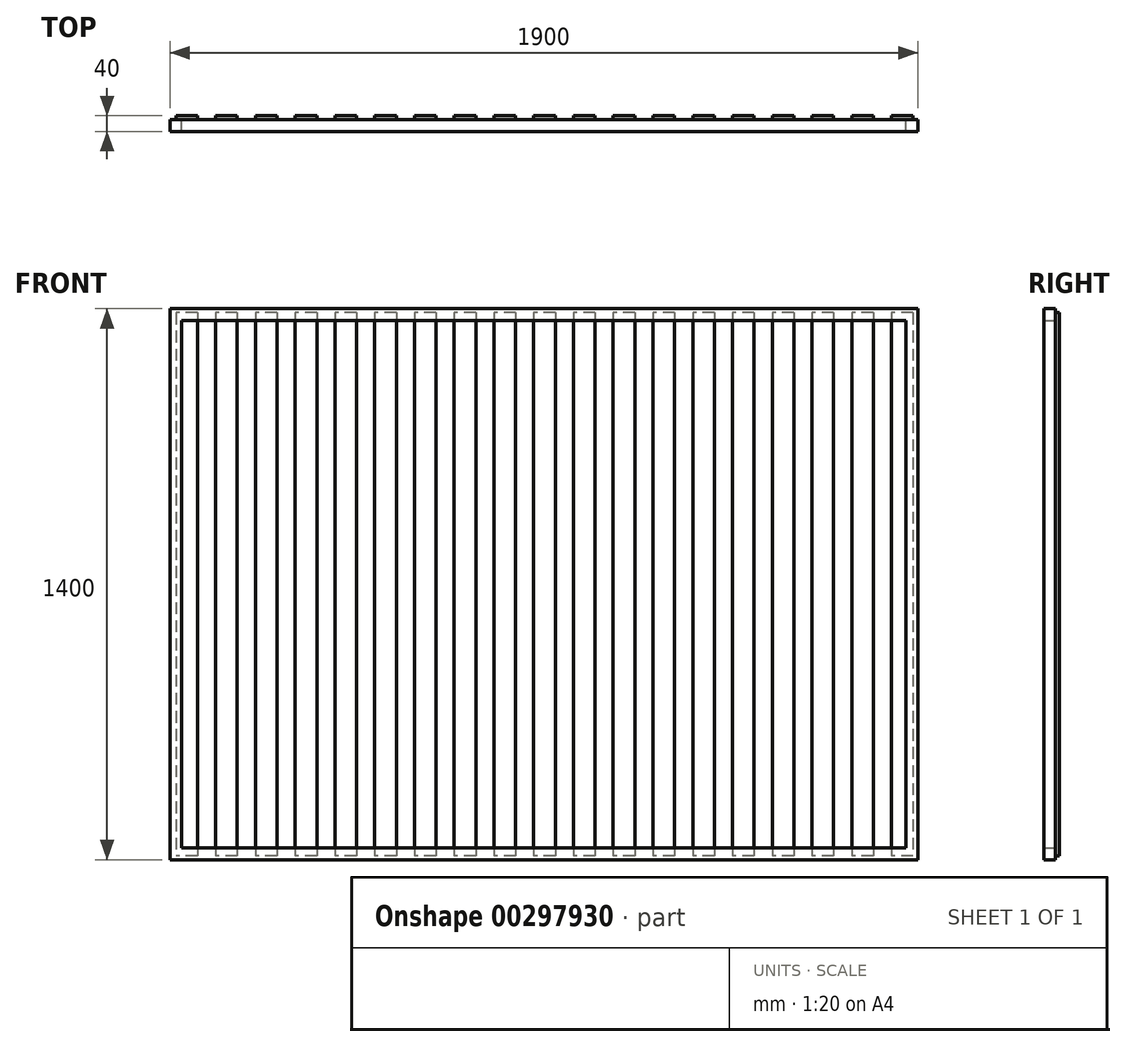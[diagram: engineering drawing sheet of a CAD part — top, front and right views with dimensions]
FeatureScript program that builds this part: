
annotation { "Feature Type Name" : "Feature", "Feature Type Description" : "" }
export const myFeature = defineFeature(function(context is Context, id is Id, definition is map)
    precondition{}
    {
        {
            var Q0;
            Q0=qCreatedBy(makeId("Front.planeOp"),FACE);
            var sketch = newSketch(context, id + "F0", { "sketchPlane" : qUnion([Q0])});
            skLineSegment(sketch, "E0.bottom", {"start": v(950, 700) * mm, "end": v(-950, 700) * mm});
            skLineSegment(sketch, "E0.top", {"start": v(950, -700) * mm, "end": v(-950, -700) * mm});
            skLineSegment(sketch, "E0.left", {"start": v(950, 700) * mm, "end": v(950, -700) * mm});
            skLineSegment(sketch, "E0.right", {"start": v(-950, 700) * mm, "end": v(-950, -700) * mm});
            skPoint(sketch, "E0.middle", {"position": v(0, 0) * mm});
            skLineSegment(sketch, "E1.bottom", {"start": v(-920, 670) * mm, "end": v(920, 670) * mm});
            skLineSegment(sketch, "E1.top", {"start": v(-920, -670) * mm, "end": v(920, -670) * mm});
            skLineSegment(sketch, "E1.left", {"start": v(-920, 670) * mm, "end": v(-920, -670) * mm});
            skLineSegment(sketch, "E1.right", {"start": v(920, 670) * mm, "end": v(920, -670) * mm});
            skSolve(sketch);
        }
        {
            var Q0;
            Q0=makeQuery(id+"F0.imprint","IMPRINT",FACE,{"disambiguationData":[TD([[makeQuery(id+"F0.imprint","IMPRINT",EDGE,{"derivedFrom":sQuery(id+"F0.wireOp",EDGE,"E0.bottom")}),1.0]])]});
            extrude(context, id + "F1", {"entities" : qUnion([Q0]), "endBound" : BoundingType.SYMMETRIC, "depth" : 30 * mm});
        }
        {
            var Q0;
            Q0=qCreatedBy(makeId("Top.planeOp"),FACE);
            var sketch = newSketch(context, id + "F2", { "sketchPlane" : qUnion([Q0])});
            skLineSegment(sketch, "E2.bottom", {"start": v(-880, 25) * mm, "end": v(-935, 25) * mm});
            skLineSegment(sketch, "E2.top", {"start": v(-880, 15) * mm, "end": v(-935, 15) * mm});
            skLineSegment(sketch, "E2.left", {"start": v(-880, 25) * mm, "end": v(-880, 15) * mm});
            skLineSegment(sketch, "E2.right", {"start": v(-935, 25) * mm, "end": v(-935, 15) * mm});
            skPoint(sketch, "E2.middle", {"position": v(-907.5, 20) * mm});
            skLineSegment(sketch, "E3.1.0.0", {"start": v(-834, 25) * mm, "end": v(-834, 15) * mm});
            skLineSegment(sketch, "E3.1.0.1", {"start": v(-779, 25) * mm, "end": v(-779, 15) * mm});
            skLineSegment(sketch, "E3.1.0.2", {"start": v(-779, 15) * mm, "end": v(-834, 15) * mm});
            skLineSegment(sketch, "E3.1.0.3", {"start": v(-779, 25) * mm, "end": v(-834, 25) * mm});
            skPoint(sketch, "E3.1.0.4", {"position": v(-806.5, 20) * mm});
            skLineSegment(sketch, "E3.2.0.0", {"start": v(-733, 25) * mm, "end": v(-733, 15) * mm});
            skLineSegment(sketch, "E3.2.0.1", {"start": v(-678, 25) * mm, "end": v(-678, 15) * mm});
            skLineSegment(sketch, "E3.2.0.2", {"start": v(-678, 15) * mm, "end": v(-733, 15) * mm});
            skLineSegment(sketch, "E3.2.0.3", {"start": v(-678, 25) * mm, "end": v(-733, 25) * mm});
            skPoint(sketch, "E3.2.0.4", {"position": v(-705.5, 20) * mm});
            skLineSegment(sketch, "E3.3.0.0", {"start": v(-632, 25) * mm, "end": v(-632, 15) * mm});
            skLineSegment(sketch, "E3.3.0.1", {"start": v(-577, 25) * mm, "end": v(-577, 15) * mm});
            skLineSegment(sketch, "E3.3.0.2", {"start": v(-577, 15) * mm, "end": v(-632, 15) * mm});
            skLineSegment(sketch, "E3.3.0.3", {"start": v(-577, 25) * mm, "end": v(-632, 25) * mm});
            skPoint(sketch, "E3.3.0.4", {"position": v(-604.5, 20) * mm});
            skLineSegment(sketch, "E3.4.0.0", {"start": v(-531, 25) * mm, "end": v(-531, 15) * mm});
            skLineSegment(sketch, "E3.4.0.1", {"start": v(-476, 25) * mm, "end": v(-476, 15) * mm});
            skLineSegment(sketch, "E3.4.0.2", {"start": v(-476, 15) * mm, "end": v(-531, 15) * mm});
            skLineSegment(sketch, "E3.4.0.3", {"start": v(-476, 25) * mm, "end": v(-531, 25) * mm});
            skPoint(sketch, "E3.4.0.4", {"position": v(-503.5, 20) * mm});
            skLineSegment(sketch, "E3.5.0.0", {"start": v(-430, 25) * mm, "end": v(-430, 15) * mm});
            skLineSegment(sketch, "E3.5.0.1", {"start": v(-375, 25) * mm, "end": v(-375, 15) * mm});
            skLineSegment(sketch, "E3.5.0.2", {"start": v(-375, 15) * mm, "end": v(-430, 15) * mm});
            skLineSegment(sketch, "E3.5.0.3", {"start": v(-375, 25) * mm, "end": v(-430, 25) * mm});
            skPoint(sketch, "E3.5.0.4", {"position": v(-402.5, 20) * mm});
            skLineSegment(sketch, "E3.6.0.0", {"start": v(-329, 25) * mm, "end": v(-329, 15) * mm});
            skLineSegment(sketch, "E3.6.0.1", {"start": v(-274, 25) * mm, "end": v(-274, 15) * mm});
            skLineSegment(sketch, "E3.6.0.2", {"start": v(-274, 15) * mm, "end": v(-329, 15) * mm});
            skLineSegment(sketch, "E3.6.0.3", {"start": v(-274, 25) * mm, "end": v(-329, 25) * mm});
            skPoint(sketch, "E3.6.0.4", {"position": v(-301.5, 20) * mm});
            skLineSegment(sketch, "E3.7.0.0", {"start": v(-228, 25) * mm, "end": v(-228, 15) * mm});
            skLineSegment(sketch, "E3.7.0.1", {"start": v(-173, 25) * mm, "end": v(-173, 15) * mm});
            skLineSegment(sketch, "E3.7.0.2", {"start": v(-173, 15) * mm, "end": v(-228, 15) * mm});
            skLineSegment(sketch, "E3.7.0.3", {"start": v(-173, 25) * mm, "end": v(-228, 25) * mm});
            skPoint(sketch, "E3.7.0.4", {"position": v(-200.5, 20) * mm});
            skLineSegment(sketch, "E3.8.0.0", {"start": v(-127, 25) * mm, "end": v(-127, 15) * mm});
            skLineSegment(sketch, "E3.8.0.1", {"start": v(-72, 25) * mm, "end": v(-72, 15) * mm});
            skLineSegment(sketch, "E3.8.0.2", {"start": v(-72, 15) * mm, "end": v(-127, 15) * mm});
            skLineSegment(sketch, "E3.8.0.3", {"start": v(-72, 25) * mm, "end": v(-127, 25) * mm});
            skPoint(sketch, "E3.8.0.4", {"position": v(-99.5, 20) * mm});
            skLineSegment(sketch, "E3.9.0.0", {"start": v(-26, 25) * mm, "end": v(-26, 15) * mm});
            skLineSegment(sketch, "E3.9.0.1", {"start": v(29, 25) * mm, "end": v(29, 15) * mm});
            skLineSegment(sketch, "E3.9.0.2", {"start": v(29, 15) * mm, "end": v(-26, 15) * mm});
            skLineSegment(sketch, "E3.9.0.3", {"start": v(29, 25) * mm, "end": v(-26, 25) * mm});
            skPoint(sketch, "E3.9.0.4", {"position": v(1.5, 20) * mm});
            skLineSegment(sketch, "E3.10.0.0", {"start": v(75, 25) * mm, "end": v(75, 15) * mm});
            skLineSegment(sketch, "E3.10.0.1", {"start": v(130, 25) * mm, "end": v(130, 15) * mm});
            skLineSegment(sketch, "E3.10.0.2", {"start": v(130, 15) * mm, "end": v(75, 15) * mm});
            skLineSegment(sketch, "E3.10.0.3", {"start": v(130, 25) * mm, "end": v(75, 25) * mm});
            skPoint(sketch, "E3.10.0.4", {"position": v(102.5, 20) * mm});
            skLineSegment(sketch, "E3.11.0.0", {"start": v(176, 25) * mm, "end": v(176, 15) * mm});
            skLineSegment(sketch, "E3.11.0.1", {"start": v(231, 25) * mm, "end": v(231, 15) * mm});
            skLineSegment(sketch, "E3.11.0.2", {"start": v(231, 15) * mm, "end": v(176, 15) * mm});
            skLineSegment(sketch, "E3.11.0.3", {"start": v(231, 25) * mm, "end": v(176, 25) * mm});
            skPoint(sketch, "E3.11.0.4", {"position": v(203.5, 20) * mm});
            skLineSegment(sketch, "E3.12.0.0", {"start": v(277, 25) * mm, "end": v(277, 15) * mm});
            skLineSegment(sketch, "E3.12.0.1", {"start": v(332, 25) * mm, "end": v(332, 15) * mm});
            skLineSegment(sketch, "E3.12.0.2", {"start": v(332, 15) * mm, "end": v(277, 15) * mm});
            skLineSegment(sketch, "E3.12.0.3", {"start": v(332, 25) * mm, "end": v(277, 25) * mm});
            skPoint(sketch, "E3.12.0.4", {"position": v(304.5, 20) * mm});
            skLineSegment(sketch, "E3.13.0.0", {"start": v(378, 25) * mm, "end": v(378, 15) * mm});
            skLineSegment(sketch, "E3.13.0.1", {"start": v(433, 25) * mm, "end": v(433, 15) * mm});
            skLineSegment(sketch, "E3.13.0.2", {"start": v(433, 15) * mm, "end": v(378, 15) * mm});
            skLineSegment(sketch, "E3.13.0.3", {"start": v(433, 25) * mm, "end": v(378, 25) * mm});
            skPoint(sketch, "E3.13.0.4", {"position": v(405.5, 20) * mm});
            skLineSegment(sketch, "E3.14.0.0", {"start": v(479, 25) * mm, "end": v(479, 15) * mm});
            skLineSegment(sketch, "E3.14.0.1", {"start": v(534, 25) * mm, "end": v(534, 15) * mm});
            skLineSegment(sketch, "E3.14.0.2", {"start": v(534, 15) * mm, "end": v(479, 15) * mm});
            skLineSegment(sketch, "E3.14.0.3", {"start": v(534, 25) * mm, "end": v(479, 25) * mm});
            skPoint(sketch, "E3.14.0.4", {"position": v(506.5, 20) * mm});
            skLineSegment(sketch, "E3.15.0.0", {"start": v(580, 25) * mm, "end": v(580, 15) * mm});
            skLineSegment(sketch, "E3.15.0.1", {"start": v(635, 25) * mm, "end": v(635, 15) * mm});
            skLineSegment(sketch, "E3.15.0.2", {"start": v(635, 15) * mm, "end": v(580, 15) * mm});
            skLineSegment(sketch, "E3.15.0.3", {"start": v(635, 25) * mm, "end": v(580, 25) * mm});
            skPoint(sketch, "E3.15.0.4", {"position": v(607.5, 20) * mm});
            skLineSegment(sketch, "E3.16.0.0", {"start": v(681, 25) * mm, "end": v(681, 15) * mm});
            skLineSegment(sketch, "E3.16.0.1", {"start": v(736, 25) * mm, "end": v(736, 15) * mm});
            skLineSegment(sketch, "E3.16.0.2", {"start": v(736, 15) * mm, "end": v(681, 15) * mm});
            skLineSegment(sketch, "E3.16.0.3", {"start": v(736, 25) * mm, "end": v(681, 25) * mm});
            skPoint(sketch, "E3.16.0.4", {"position": v(708.5, 20) * mm});
            skLineSegment(sketch, "E3.17.0.0", {"start": v(782, 25) * mm, "end": v(782, 15) * mm});
            skLineSegment(sketch, "E3.17.0.1", {"start": v(837, 25) * mm, "end": v(837, 15) * mm});
            skLineSegment(sketch, "E3.17.0.2", {"start": v(837, 15) * mm, "end": v(782, 15) * mm});
            skLineSegment(sketch, "E3.17.0.3", {"start": v(837, 25) * mm, "end": v(782, 25) * mm});
            skPoint(sketch, "E3.17.0.4", {"position": v(809.5, 20) * mm});
            skLineSegment(sketch, "E3.18.0.0", {"start": v(883, 25) * mm, "end": v(883, 15) * mm});
            skLineSegment(sketch, "E3.18.0.1", {"start": v(938, 25) * mm, "end": v(938, 15) * mm});
            skLineSegment(sketch, "E3.18.0.2", {"start": v(938, 15) * mm, "end": v(883, 15) * mm});
            skLineSegment(sketch, "E3.18.0.3", {"start": v(938, 25) * mm, "end": v(883, 25) * mm});
            skPoint(sketch, "E3.18.0.4", {"position": v(910.5, 20) * mm});
            skLineSegment(sketch, "E3.direction1", {"start": v(-935, 15) * mm, "end": v(-834, 15) * mm, "construction": true});
            skSolve(sketch);
        }
        {
            var Q0;
            Q0=makeQuery(id+"F2.imprint","IMPRINT",FACE,{"disambiguationData":[TD([[makeQuery(id+"F2.imprint","IMPRINT",EDGE,{"derivedFrom":sQuery(id+"F2.wireOp",EDGE,"E2.bottom")}),1.0]])]});
            var Q1;
            Q1=makeQuery(id+"F2.imprint","IMPRINT",FACE,{"disambiguationData":[TD([[makeQuery(id+"F2.imprint","IMPRINT",EDGE,{"derivedFrom":sQuery(id+"F2.wireOp",EDGE,"E3.1.0.0")}),1.0]])]});
            var Q2;
            Q2=makeQuery(id+"F2.imprint","IMPRINT",FACE,{"disambiguationData":[TD([[makeQuery(id+"F2.imprint","IMPRINT",EDGE,{"derivedFrom":sQuery(id+"F2.wireOp",EDGE,"E3.2.0.0")}),1.0]])]});
            var Q3;
            Q3=makeQuery(id+"F2.imprint","IMPRINT",FACE,{"disambiguationData":[TD([[makeQuery(id+"F2.imprint","IMPRINT",EDGE,{"derivedFrom":sQuery(id+"F2.wireOp",EDGE,"E3.3.0.0")}),1.0]])]});
            var Q4;
            Q4=makeQuery(id+"F2.imprint","IMPRINT",FACE,{"disambiguationData":[TD([[makeQuery(id+"F2.imprint","IMPRINT",EDGE,{"derivedFrom":sQuery(id+"F2.wireOp",EDGE,"E3.4.0.0")}),1.0]])]});
            var Q5;
            Q5=makeQuery(id+"F2.imprint","IMPRINT",FACE,{"disambiguationData":[TD([[makeQuery(id+"F2.imprint","IMPRINT",EDGE,{"derivedFrom":sQuery(id+"F2.wireOp",EDGE,"E3.5.0.0")}),1.0]])]});
            var Q6;
            Q6=makeQuery(id+"F2.imprint","IMPRINT",FACE,{"disambiguationData":[TD([[makeQuery(id+"F2.imprint","IMPRINT",EDGE,{"derivedFrom":sQuery(id+"F2.wireOp",EDGE,"E3.6.0.0")}),1.0]])]});
            var Q7;
            Q7=makeQuery(id+"F2.imprint","IMPRINT",FACE,{"disambiguationData":[TD([[makeQuery(id+"F2.imprint","IMPRINT",EDGE,{"derivedFrom":sQuery(id+"F2.wireOp",EDGE,"E3.7.0.0")}),1.0]])]});
            var Q8;
            Q8=makeQuery(id+"F2.imprint","IMPRINT",FACE,{"disambiguationData":[TD([[makeQuery(id+"F2.imprint","IMPRINT",EDGE,{"derivedFrom":sQuery(id+"F2.wireOp",EDGE,"E3.8.0.0")}),1.0]])]});
            var Q9;
            Q9=makeQuery(id+"F2.imprint","IMPRINT",FACE,{"disambiguationData":[TD([[makeQuery(id+"F2.imprint","IMPRINT",EDGE,{"derivedFrom":sQuery(id+"F2.wireOp",EDGE,"E3.9.0.0")}),1.0]])]});
            var Q10;
            Q10=makeQuery(id+"F2.imprint","IMPRINT",FACE,{"disambiguationData":[TD([[makeQuery(id+"F2.imprint","IMPRINT",EDGE,{"derivedFrom":sQuery(id+"F2.wireOp",EDGE,"E3.10.0.0")}),1.0]])]});
            var Q11;
            Q11=makeQuery(id+"F2.imprint","IMPRINT",FACE,{"disambiguationData":[TD([[makeQuery(id+"F2.imprint","IMPRINT",EDGE,{"derivedFrom":sQuery(id+"F2.wireOp",EDGE,"E3.11.0.0")}),1.0]])]});
            var Q12;
            Q12=makeQuery(id+"F2.imprint","IMPRINT",FACE,{"disambiguationData":[TD([[makeQuery(id+"F2.imprint","IMPRINT",EDGE,{"derivedFrom":sQuery(id+"F2.wireOp",EDGE,"E3.12.0.0")}),1.0]])]});
            var Q13;
            Q13=makeQuery(id+"F2.imprint","IMPRINT",FACE,{"disambiguationData":[TD([[makeQuery(id+"F2.imprint","IMPRINT",EDGE,{"derivedFrom":sQuery(id+"F2.wireOp",EDGE,"E3.13.0.0")}),1.0]])]});
            var Q14;
            Q14=makeQuery(id+"F2.imprint","IMPRINT",FACE,{"disambiguationData":[TD([[makeQuery(id+"F2.imprint","IMPRINT",EDGE,{"derivedFrom":sQuery(id+"F2.wireOp",EDGE,"E3.14.0.0")}),1.0]])]});
            var Q15;
            Q15=makeQuery(id+"F2.imprint","IMPRINT",FACE,{"disambiguationData":[TD([[makeQuery(id+"F2.imprint","IMPRINT",EDGE,{"derivedFrom":sQuery(id+"F2.wireOp",EDGE,"E3.15.0.0")}),1.0]])]});
            var Q16;
            Q16=makeQuery(id+"F2.imprint","IMPRINT",FACE,{"disambiguationData":[TD([[makeQuery(id+"F2.imprint","IMPRINT",EDGE,{"derivedFrom":sQuery(id+"F2.wireOp",EDGE,"E3.16.0.0")}),1.0]])]});
            var Q17;
            Q17=makeQuery(id+"F2.imprint","IMPRINT",FACE,{"disambiguationData":[TD([[makeQuery(id+"F2.imprint","IMPRINT",EDGE,{"derivedFrom":sQuery(id+"F2.wireOp",EDGE,"E3.17.0.0")}),1.0]])]});
            var Q18;
            Q18=makeQuery(id+"F2.imprint","IMPRINT",FACE,{"disambiguationData":[TD([[makeQuery(id+"F2.imprint","IMPRINT",EDGE,{"derivedFrom":sQuery(id+"F2.wireOp",EDGE,"E3.18.0.0")}),1.0]])]});
            var Q19;
            Q19=makeQuery(id+"F2.imprint","IMPRINT",FACE,{"disambiguationData":[TD([[makeQuery(id+"F2.imprint","IMPRINT",EDGE,{"derivedFrom":sQuery(id+"F2.wireOp",EDGE,"E3.19.0.0")}),1.0]])]});
            var Q20;
            Q20=makeQuery(id+"F2.imprint","IMPRINT",FACE,{"disambiguationData":[TD([[makeQuery(id+"F2.imprint","IMPRINT",EDGE,{"derivedFrom":sQuery(id+"F2.wireOp",EDGE,"E3.20.0.0")}),1.0]])]});
            var Q21;
            Q21=makeQuery(id+"F2.imprint","IMPRINT",FACE,{"disambiguationData":[TD([[makeQuery(id+"F2.imprint","IMPRINT",EDGE,{"derivedFrom":sQuery(id+"F2.wireOp",EDGE,"E3.21.0.0")}),1.0]])]});
            var Q22;
            Q22=makeQuery(id+"F2.imprint","IMPRINT",FACE,{"disambiguationData":[TD([[makeQuery(id+"F2.imprint","IMPRINT",EDGE,{"derivedFrom":sQuery(id+"F2.wireOp",EDGE,"E3.22.0.0")}),1.0]])]});
            var Q23;
            Q23=makeQuery(id+"F2.imprint","IMPRINT",FACE,{"disambiguationData":[TD([[makeQuery(id+"F2.imprint","IMPRINT",EDGE,{"derivedFrom":sQuery(id+"F2.wireOp",EDGE,"E3.23.0.0")}),1.0]])]});
            var Q24;
            Q24=makeQuery(id+"F2.imprint","IMPRINT",FACE,{"disambiguationData":[TD([[makeQuery(id+"F2.imprint","IMPRINT",EDGE,{"derivedFrom":sQuery(id+"F2.wireOp",EDGE,"E3.24.0.0")}),1.0]])]});
            var Q25;
            Q25=makeQuery(id+"F2.imprint","IMPRINT",FACE,{"disambiguationData":[TD([[makeQuery(id+"F2.imprint","IMPRINT",EDGE,{"derivedFrom":sQuery(id+"F2.wireOp",EDGE,"E3.25.0.0")}),1.0]])]});
            var Q26;
            Q26=makeQuery(id+"F2.imprint","IMPRINT",FACE,{"disambiguationData":[TD([[makeQuery(id+"F2.imprint","IMPRINT",EDGE,{"derivedFrom":sQuery(id+"F2.wireOp",EDGE,"E3.26.0.0")}),1.0]])]});
            var Q27;
            Q27=makeQuery(id+"F2.imprint","IMPRINT",FACE,{"disambiguationData":[TD([[makeQuery(id+"F2.imprint","IMPRINT",EDGE,{"derivedFrom":sQuery(id+"F2.wireOp",EDGE,"E3.28.0.0")}),1.0]])]});
            var Q28;
            Q28=makeQuery(id+"F2.imprint","IMPRINT",FACE,{"disambiguationData":[TD([[makeQuery(id+"F2.imprint","IMPRINT",EDGE,{"derivedFrom":sQuery(id+"F2.wireOp",EDGE,"E3.29.0.0")}),1.0]])]});
            var Q29;
            Q29=makeQuery(id+"F2.imprint","IMPRINT",FACE,{"disambiguationData":[TD([[makeQuery(id+"F2.imprint","IMPRINT",EDGE,{"derivedFrom":sQuery(id+"F2.wireOp",EDGE,"E3.27.0.0")}),1.0]])]});
            var Q30;
            Q30=makeQuery(id+"F2.imprint","IMPRINT",FACE,{"disambiguationData":[TD([[makeQuery(id+"F2.imprint","IMPRINT",EDGE,{"derivedFrom":sQuery(id+"F2.wireOp",EDGE,"E3.30.0.0")}),1.0]])]});
            var Q31;
            Q31=makeQuery(id+"F2.imprint","IMPRINT",FACE,{"disambiguationData":[TD([[makeQuery(id+"F2.imprint","IMPRINT",EDGE,{"derivedFrom":sQuery(id+"F2.wireOp",EDGE,"E3.31.0.0")}),1.0]])]});
            var Q32;
            Q32=makeQuery(id+"F2.imprint","IMPRINT",FACE,{"disambiguationData":[TD([[makeQuery(id+"F2.imprint","IMPRINT",EDGE,{"derivedFrom":sQuery(id+"F2.wireOp",EDGE,"E3.32.0.0")}),1.0]])]});
            extrude(context, id + "F3", {"entities" : qUnion([Q0, Q1, Q2, Q3, Q4, Q5, Q6, Q7, Q8, Q9, Q10, Q11, Q12, Q13, Q14, Q15, Q16, Q17, Q18, Q19, Q20, Q21, Q22, Q23, Q24, Q25, Q26, Q27, Q28, Q29, Q30, Q31, Q32]), "operationType" : NewBodyOperationType.ADD, "endBound" : BoundingType.SYMMETRIC, "depth" : 1380 * mm});
        }
    });
